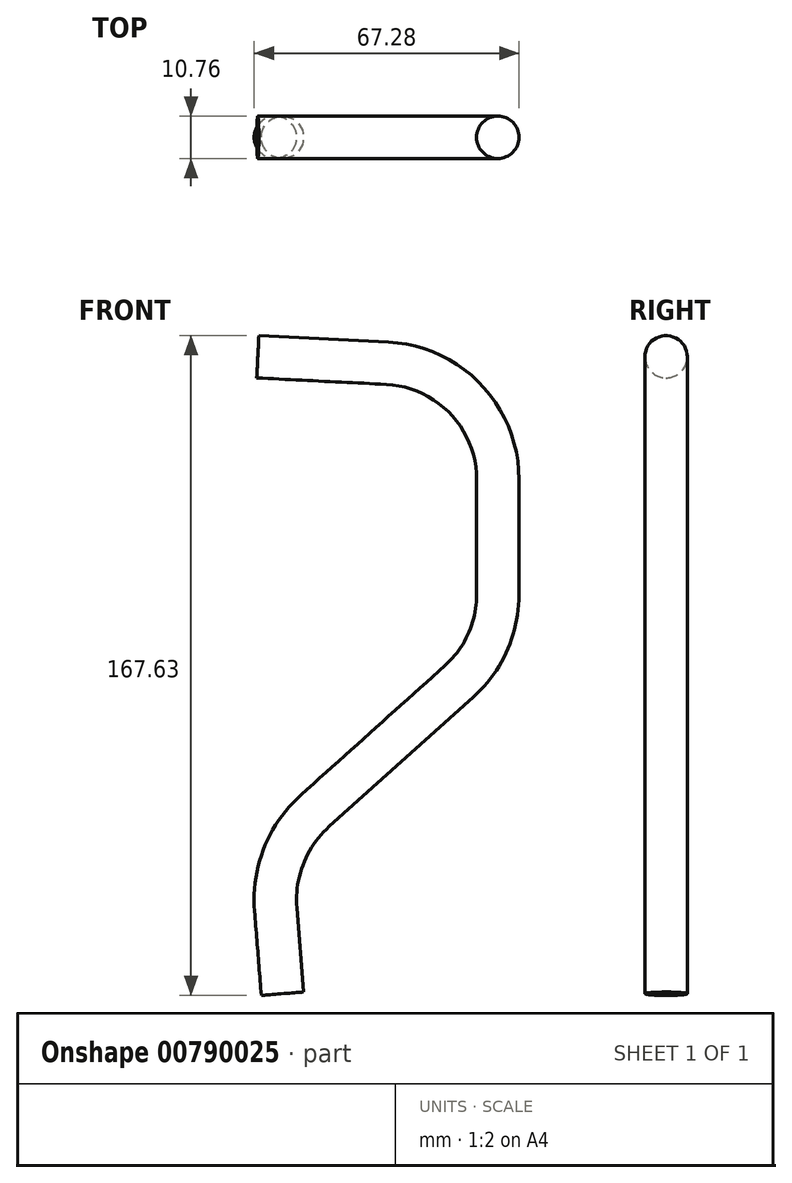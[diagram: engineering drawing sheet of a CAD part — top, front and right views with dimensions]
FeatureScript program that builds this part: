
annotation { "Feature Type Name" : "Feature", "Feature Type Description" : "" }
export const myFeature = defineFeature(function(context is Context, id is Id, definition is map)
    precondition{}
    {
        {
            var Q0;
            Q0=qCreatedBy(makeId("Front.planeOp"),FACE);
            var sketch = newSketch(context, id + "F0", { "sketchPlane" : qUnion([Q0])});
            skLineSegment(sketch, "E0", {"start": v(-26.7, 95.48) * mm, "end": v(6.23, 93.82) * mm});
            skLineSegment(sketch, "E1", {"start": v(34.72, 63.85) * mm, "end": v(34.72, 34.51) * mm});
            skLineSegment(sketch, "E2", {"start": v(24.77, 12.2) * mm, "end": v(-11.85, -20.71) * mm});
            skLineSegment(sketch, "E3", {"start": v(-21.7, -45.4) * mm, "end": v(-20, -66.8) * mm});
            skPoint(sketch, "E4.visualSharp", {"position": v(34.72, 92.38) * mm});
            skArc(sketch, "E4.filletArc", {"start": v(34.72, 63.85) * mm, "mid": v(26.46, 84.53) * mm, "end": v(6.23, 93.82) * mm});
            skPoint(sketch, "E5.visualSharp", {"position": v(34.72, 21.14) * mm});
            skArc(sketch, "E5.filletArc", {"start": v(24.77, 12.2) * mm, "mid": v(32.12, 22.3) * mm, "end": v(34.72, 34.51) * mm});
            skPoint(sketch, "E6.visualSharp", {"position": v(-22.88, -30.62) * mm});
            skArc(sketch, "E6.filletArc", {"start": v(-11.85, -20.71) * mm, "mid": v(-19.66, -31.9) * mm, "end": v(-21.7, -45.4) * mm});
            skSolve(sketch);
        }
        {
            var Q0;
            Q0=sQuery(id+"F0.wireOp",EDGE,"E3");
            var Q1;
            Q1=sQuery(id+"F0.wireOp",VERTEX,"E3.end");
            cPlane(context, id + "F1", {"entities" : qUnion([Q0, Q1]), "cplaneType" : CPlaneType.LINE_POINT, "offset" : 25 * mm, "width" : 150 * mm, "height" : 150 * mm});
        }
        {
            var Q0;
            Q0=qCreatedBy(id+"F1.planeOp",FACE);
            var sketch = newSketch(context, id + "F2", { "sketchPlane" : qUnion([Q0])});
            skCircle(sketch, "E7", {"center": v(-25.71, 0) * mm, "radius": 5.38 * mm});
            skSolve(sketch);
        }
        {
            var Q0;
            Q0=makeQuery(id+"F2.imprint","IMPRINT",FACE,{"disambiguationData":[TD([[makeQuery(id+"F2.imprint","IMPRINT",EDGE,{"derivedFrom":sQuery(id+"F2.wireOp",EDGE,"E7")}),1.0]])]});
            var Q1;
            Q1=sQuery(id+"F0.wireOp",EDGE,"E0");
            var Q2;
            Q2=sQuery(id+"F0.wireOp",EDGE,"E4.filletArc");
            var Q3;
            Q3=sQuery(id+"F0.wireOp",EDGE,"E1");
            var Q4;
            Q4=sQuery(id+"F0.wireOp",EDGE,"E5.filletArc");
            var Q5;
            Q5=sQuery(id+"F0.wireOp",EDGE,"E2");
            var Q6;
            Q6=sQuery(id+"F0.wireOp",EDGE,"E6.filletArc");
            var Q7;
            Q7=sQuery(id+"F0.wireOp",EDGE,"E3");
            sweep(context, id + "F3", {"profiles" : qUnion([Q0]), "path" : qUnion([Q1, Q2, Q3, Q4, Q5, Q6, Q7])});
        }
    });
